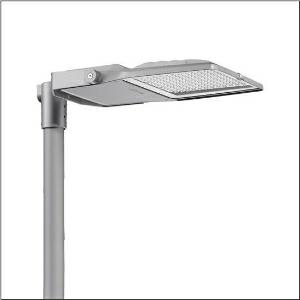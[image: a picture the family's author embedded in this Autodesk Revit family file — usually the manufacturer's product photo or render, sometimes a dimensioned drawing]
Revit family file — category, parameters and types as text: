
# Revit family: floodlight_fl_21_iq_midi___pl64_5xa7781f4e3a_1626
name_source: partatom
category: Lighting Fixtures
units: mm (PartAtom-declared; Revit-internal decimal feet)

## family parameters
Cut with Voids When Loaded = No
Host = Face
Light Source = No
Part Type = Normal
Room Calculation Point = No
Round Connector Dimension = Use Diameter
Shared = No

## types (1)
- --- (1 x LED, 36050 lm, 270.2 W, 4000K)
    Apparent Load = 270 VA
    CIE Flux Codes = 28 80 98 100 100
    Color Rendering = 70
    Color Temperature = 4000K
    Default Elevation = 1800 mm
    Description = Floodlight FL 21 iQ midi, floodlight, primary light control with lens, of PMMA, primary optical cover: protective disc, of toughened safety glass, transparent, light distribution: PL64, light emission: direct distribution, installation type: surface-mounted, lamps: LED, High Power LED, rated values: 36.050lm | 270,2W | 133,4lm/W (begin service life); end service life: 36.050lm | 286,6W; at 50% lumin. flux: 18.025lm | 117,7W | 153,1lm/W, colour temperature: 4000K, colour rendering: CRI > 70, light colour: 740, light setting 1 begin service life: 100% | 36.050lm | 270,2W | 133,4lm/W | 4.000K, light setting 1 end service life: 286,6W, further light settings possible, control: optimised constant luminous flux control (CLO 2.0), Desk-Remote (wireless, voltage-free reading and setting of iQ features in the workshop via application-optimized NFC function/RFID function), Light-Fading, Smart-Wire, Night-Set, Lumen-Switch, Temp-Guard, Auto-Match, pre-setting: linear dimming characteristic, with terminal, 6-pole, mains connection: 220..240V, AC, 50/60Hz, luminaire housing, of diecast aluminium, powder-coated, SITECO metallic grey (DB 702S), corrosivity category C5 mid according to DIN EN ISO 12944suitable for swimming poolschlorine-resistant, sealing non-destructively replaceable, please order mast flange separately, mast bracket, of steel, galvanised, powder-coated, SITECO metallic grey (DB 702S), protection rating (complete): IP66, insulation class (complete): insulation class II (safety insulation), certification: CE, ENEC, VDE, protection symbol: D, impact resistance: IK08, permissible operating ambient temperature: -40..+40°C, permissible operating ambient temperature for outdoor applications: -40..+50°C, standard: DIN EN 12944, LABS conformity tested according to VDMA 24364:2018-05, packaging unit: 1 piece

Light Distribution: PL64
    Height = 76 mm
    Lamp = 1 x LED
    Lamp Light Flux = 36050 lm
    Lamp Power = 270.2 W
    Lamp count = 1
    Length = 657 mm
    Luminous efficacy = 133 lm/W
    Manufacturer = Siteco
    ModVariant = No
    Model = 5XA7781F4E3A
    Number of Poles = 1
    OnlyDefault = Yes
    Power Factor = 1
    Product Name = Floodlight FL 21 iQ midi | PL64
    Product group = floodlight | pylon annexe
    ProductGroupID = 6201
    Protection Class = Protection class II
    Protection Degree = IP 66
    RLX_Detail_Level = 1
    RLX_Emergency_Light_Flux = 0 lm
    RLX_Emergency_Type = 0
    RLX_Emergency_Type_DB = No
    RlxData = <blob elided: 154053 chars, md5=76eb3f75>
    Socket = socket
    Standby Power = 0 W
    System Light Flux = 36050 lm
    System Power = 270 W
    Type Comments = factory setting: luminous flux: 100 % | dim-lin: 254 | 620 mA
    Type Image = l_1007123.jpg
    URL = http://relux.com
    VarID = @adj_106737
    Voltage = 0 V
    Weight = 0.00 kg
    Width = 442 mm

## geometry (parser evidence)
native form markers: Blend x4, Sweep x13
no freeform markers — native parametric forms only
